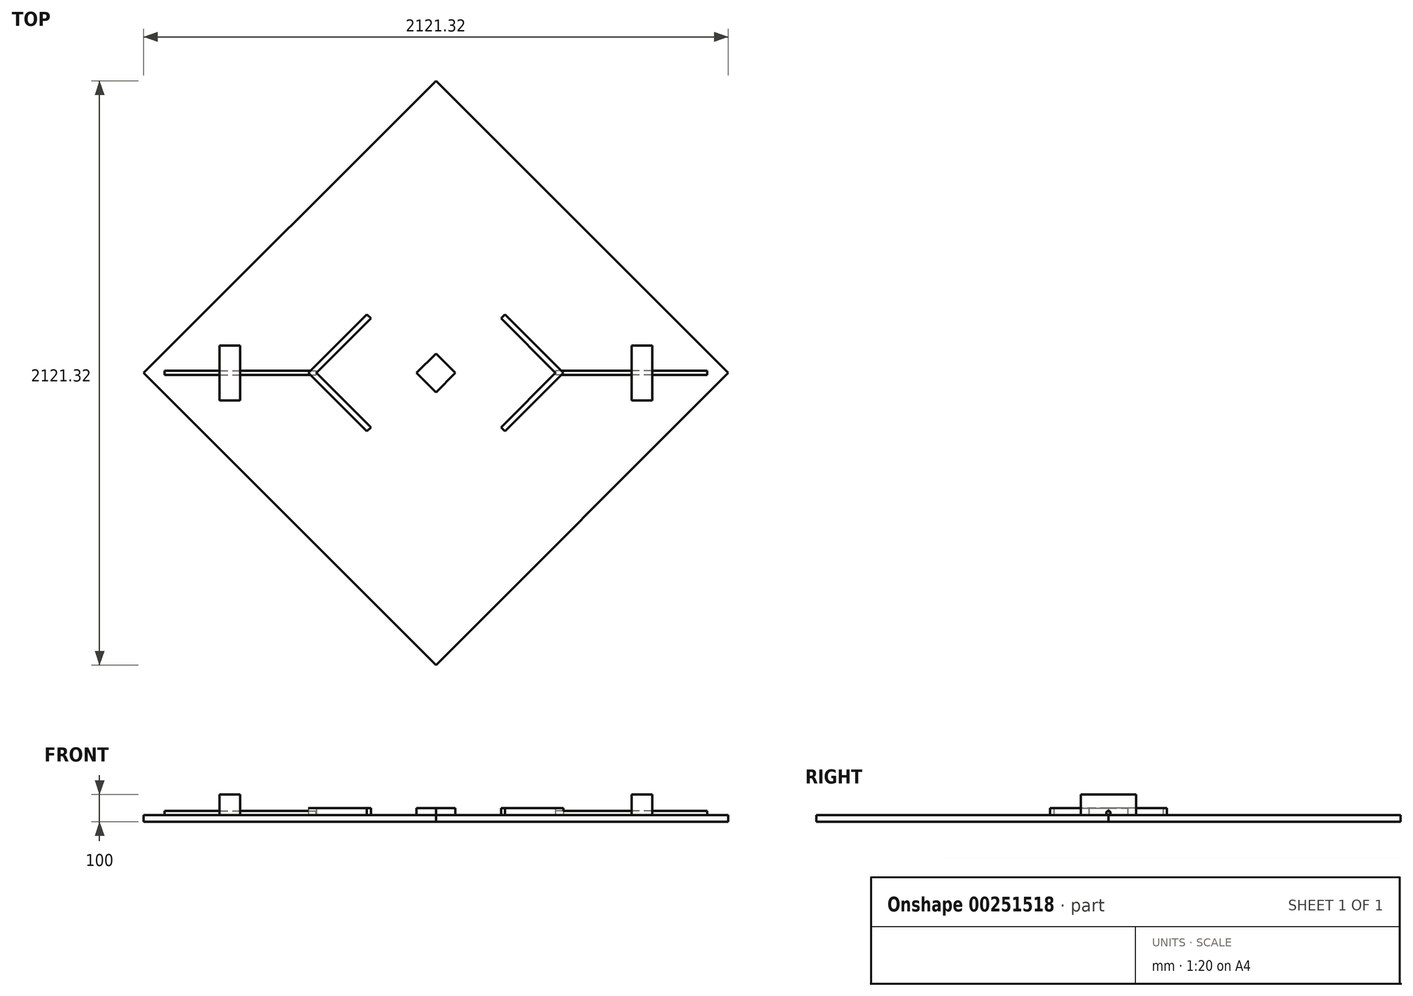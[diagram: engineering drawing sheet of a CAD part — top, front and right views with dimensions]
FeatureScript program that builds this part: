
annotation { "Feature Type Name" : "Feature", "Feature Type Description" : "" }
export const myFeature = defineFeature(function(context is Context, id is Id, definition is map)
    precondition{}
    {
        {
            var Q0;
            Q0=qCreatedBy(makeId("Top.planeOp"),FACE);
            var sketch = newSketch(context, id + "F0", { "sketchPlane" : qUnion([Q0])});
            skLineSegment(sketch, "E0", {"start": v(-424.26, 0) * mm, "end": v(0, 424.26) * mm, "construction": true});
            skLineSegment(sketch, "E1", {"start": v(0, 424.26) * mm, "end": v(424.26, 0) * mm, "construction": true});
            skLineSegment(sketch, "E2", {"start": v(424.26, 0) * mm, "end": v(0, -424.26) * mm, "construction": true});
            skLineSegment(sketch, "E3", {"start": v(0, -424.26) * mm, "end": v(-424.26, 0) * mm, "construction": true});
            skCircle(sketch, "E4", {"center": v(-424.26, 0) * mm, "radius": 225 * mm, "construction": true});
            skCircle(sketch, "E5", {"center": v(0, 424.26) * mm, "radius": 225 * mm, "construction": true});
            skCircle(sketch, "E6", {"center": v(424.26, 0) * mm, "radius": 225 * mm, "construction": true});
            skCircle(sketch, "E7", {"center": v(0, -424.26) * mm, "radius": 225 * mm, "construction": true});
            skSolve(sketch);
        }
        {
            var Q0;
            Q0=qCreatedBy(makeId("Top.planeOp"),FACE);
            var sketch = newSketch(context, id + "F1", { "sketchPlane" : qUnion([Q0])});
            skLineSegment(sketch, "E8", {"start": v(-70.71, 0) * mm, "end": v(0, 70.71) * mm});
            skLineSegment(sketch, "E9", {"start": v(0, 70.71) * mm, "end": v(70.71, 0) * mm});
            skLineSegment(sketch, "E10", {"start": v(70.71, 0) * mm, "end": v(0, -70.71) * mm});
            skLineSegment(sketch, "E11", {"start": v(0, -70.71) * mm, "end": v(-70.71, 0) * mm});
            skSolve(sketch);
        }
        {
            var Q0;
            Q0=qCreatedBy(makeId("Top.planeOp"),FACE);
            var sketch = newSketch(context, id + "F2", { "sketchPlane" : qUnion([Q0])});
            skLineSegment(sketch, "E12", {"start": v(-1060.66, 0) * mm, "end": v(0, 1060.66) * mm});
            skLineSegment(sketch, "E13", {"start": v(0, 1060.66) * mm, "end": v(1060.66, 0) * mm});
            skLineSegment(sketch, "E14", {"start": v(1060.66, 0) * mm, "end": v(0, -1060.66) * mm});
            skLineSegment(sketch, "E15", {"start": v(0, -1060.66) * mm, "end": v(-1060.66, 0) * mm});
            skSolve(sketch);
        }
        {
            var Q0;
            Q0=qCreatedBy(makeId("Top.planeOp"),FACE);
            var sketch = newSketch(context, id + "F3", { "sketchPlane" : qUnion([Q0])});
            skLineSegment(sketch, "E16.bottom", {"start": v(784.96, 100) * mm, "end": v(709.96, 100) * mm});
            skLineSegment(sketch, "E16.top", {"start": v(784.96, -100) * mm, "end": v(709.96, -100) * mm});
            skLineSegment(sketch, "E16.left", {"start": v(784.96, 100) * mm, "end": v(784.96, -100) * mm});
            skLineSegment(sketch, "E16.right", {"start": v(709.96, 100) * mm, "end": v(709.96, -100) * mm});
            skPoint(sketch, "E16.middle", {"position": v(747.46, 0) * mm});
            skLineSegment(sketch, "E17", {"start": v(236.27, 197.99) * mm, "end": v(434.26, 0) * mm});
            skLineSegment(sketch, "E18", {"start": v(434.26, 0) * mm, "end": v(236.27, -197.99) * mm});
            skLineSegment(sketch, "E19", {"start": v(747.46, 0) * mm, "end": v(434.26, 0) * mm, "construction": true});
            skLineSegment(sketch, "E20", {"start": v(236.27, 197.99) * mm, "end": v(250.42, 212.13) * mm});
            skLineSegment(sketch, "E21", {"start": v(250.42, 212.13) * mm, "end": v(462.55, 0) * mm});
            skLineSegment(sketch, "E22", {"start": v(236.27, -197.99) * mm, "end": v(250.42, -212.13) * mm});
            skLineSegment(sketch, "E23", {"start": v(250.42, -212.13) * mm, "end": v(462.55, 0) * mm});
            skPoint(sketch, "E24.0", {"position": v(424.26, 0) * mm});
            skPoint(sketch, "E25.0", {"position": v(1060.66, 0) * mm});
            skLineSegment(sketch, "E26", {"start": v(1060.66, 0) * mm, "end": v(747.46, 0) * mm, "construction": true});
            skSolve(sketch);
        }
        {
            var Q0;
            Q0 = qSketchRegion(id + "F2", true);
            extrude(context, id + "F4", {"entities" : qUnion([Q0]), "oppositeDirection" : true, "depth" : 25 * mm});
        }
        {
            var Q0;
            Q0=makeQuery(id+"F4.opExtrude","CAP_FACE",FACE,{"disambiguationData":[OSD([sQuery(id+"F2.wireOp",EDGE,"E12"),sQuery(id+"F2.wireOp",EDGE,"E13"),sQuery(id+"F2.wireOp",EDGE,"E14"),sQuery(id+"F2.wireOp",EDGE,"E15")])],"isStart":true});
            var sketch = newSketch(context, id + "F5", { "sketchPlane" : qUnion([Q0])});
            skLineSegment(sketch, "E27.0", {"start": v(784.96, -100) * mm, "end": v(709.96, -100) * mm});
            skLineSegment(sketch, "E27.1", {"start": v(784.96, 100) * mm, "end": v(784.96, -100) * mm});
            skLineSegment(sketch, "E27.2", {"start": v(709.96, 100) * mm, "end": v(709.96, -100) * mm});
            skLineSegment(sketch, "E27.3", {"start": v(784.96, 100) * mm, "end": v(709.96, 100) * mm});
            skSolve(sketch);
        }
        {
            var Q0;
            Q0 = qSketchRegion(id + "F5", true);
            extrude(context, id + "F6", {"entities" : qUnion([Q0]), "depth" : 75 * mm});
        }
        {
            var Q0;
            Q0=makeQuery(id+"F4.opExtrude","CAP_FACE",FACE,{"disambiguationData":[OSD([sQuery(id+"F2.wireOp",EDGE,"E12"),sQuery(id+"F2.wireOp",EDGE,"E13"),sQuery(id+"F2.wireOp",EDGE,"E14"),sQuery(id+"F2.wireOp",EDGE,"E15")])],"isStart":true});
            var sketch = newSketch(context, id + "F7", { "sketchPlane" : qUnion([Q0])});
            skLineSegment(sketch, "E28.0", {"start": v(250.42, -212.13) * mm, "end": v(462.55, 0) * mm});
            skLineSegment(sketch, "E28.1", {"start": v(236.27, -197.99) * mm, "end": v(250.42, -212.13) * mm});
            skLineSegment(sketch, "E28.2", {"start": v(434.26, 0) * mm, "end": v(236.27, -197.99) * mm});
            skLineSegment(sketch, "E28.3", {"start": v(236.27, 197.99) * mm, "end": v(434.26, 0) * mm});
            skLineSegment(sketch, "E28.4", {"start": v(250.42, 212.13) * mm, "end": v(462.55, 0) * mm});
            skLineSegment(sketch, "E28.5", {"start": v(236.27, 197.99) * mm, "end": v(250.42, 212.13) * mm});
            skSolve(sketch);
        }
        {
            var Q0;
            Q0 = qSketchRegion(id + "F7", true);
            extrude(context, id + "F8", {"entities" : qUnion([Q0]), "depth" : 25 * mm});
        }
        {
            var Q0;
            Q0=makeQuery(id+"F6.opExtrude","SWEPT_FACE",FACE,{"disambiguationData":[OSD([sQuery(id+"F5.wireOp",EDGE,"E27.1")])]});
            var sketch = newSketch(context, id + "F9", { "sketchPlane" : qUnion([Q0])});
            skCircle(sketch, "E29", {"center": v(0, 7.5) * mm, "radius": 7.5 * mm});
            skSolve(sketch);
        }
        {
            var Q0;
            Q0 = qSketchRegion(id + "F9", true);
            extrude(context, id + "F10", {"entities" : qUnion([Q0]), "depth" : 200 * mm, "hasSecondDirection" : true, "secondDirectionOppositeDirection" : true, "secondDirectionDepth" : 350 * mm});
        }
        {
            var Q0;
            Q0 = qSketchRegion(id + "F1", true);
            extrude(context, id + "F11", {"entities" : qUnion([Q0]), "depth" : 25 * mm});
        }
        {
            var Q0;
            Q0=makeQuery(id+"F8.opExtrude","SWEPT_BODY",BODY,{"disambiguationData":[OSD([sQuery(id+"F7.wireOp",EDGE,"E28.0"),sQuery(id+"F7.wireOp",EDGE,"E28.1"),sQuery(id+"F7.wireOp",EDGE,"E28.2"),sQuery(id+"F7.wireOp",EDGE,"E28.3"),sQuery(id+"F7.wireOp",EDGE,"E28.4"),sQuery(id+"F7.wireOp",EDGE,"E28.5")])]});
            var Q1;
            Q1=makeQuery(id+"F10.opExtrude","SWEPT_BODY",BODY,{"disambiguationData":[OSD([sQuery(id+"F9.wireOp",EDGE,"E29")])]});
            var Q2;
            Q2=makeQuery(id+"F6.opExtrude","SWEPT_BODY",BODY,{"disambiguationData":[OSD([sQuery(id+"F5.wireOp",EDGE,"E27.0"),sQuery(id+"F5.wireOp",EDGE,"E27.1"),sQuery(id+"F5.wireOp",EDGE,"E27.2"),sQuery(id+"F5.wireOp",EDGE,"E27.3")])]});
            var Q3;
            Q3=qCreatedBy(makeId("Right.planeOp"),FACE);
            mirror(context, id + "F12", {"entities" : qUnion([Q0, Q1, Q2]), "mirrorPlane" : qUnion([Q3])});
        }
    });
